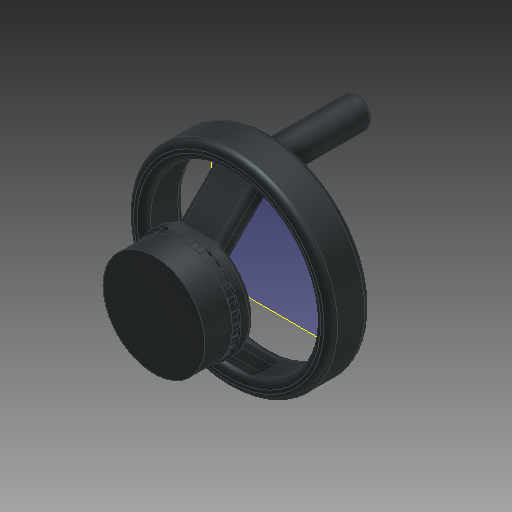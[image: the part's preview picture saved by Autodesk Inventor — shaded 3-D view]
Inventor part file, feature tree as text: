
AUTODESK INVENTOR PART (.ipt)
format: ipt  version: 2018 (Build 220112000, 112)  size: 558,080 bytes
history: native  units: mm
features: extrude x13, sketch x13, fillet x6, pattern_circular x1, chamfer x1, plane x1
ambient origin geometry x8: Origin, YZ Plane, XZ Plane, XY Plane, X Axis, Y Axis, Z Axis, Center Point
bodies: Solid1 (feature_tree)
feature tree (35):
  extrude  "Extrusion1"  Depth=20.0mm TaperAngle=0.0deg
  extrude  "Extrusion2"  Depth=5.0mm TaperAngle=0.0deg
  extrude  "Extrusion3"  Depth=5.0mm
  pattern_circular  "Circular Pattern1"  Count=30 Angle=360.0deg
  extrude  "Extrusion4"  Depth=10.0mm TaperAngle=0.0deg
  extrude  "Extrusion5"  Depth=16.0mm
  extrude  "Extrusion6"  Depth=10.0mm
  chamfer  "Chamfer1"  Distance=10.0mm
  plane  "Work Plane1"
  extrude  "Extrusion7"  Depth=2.0mm
  fillet  "Fillet1"  Radius=150.0mm
  extrude  "Extrusion8"  Depth=5.0mm TaperAngle=0.0deg
  fillet  "Fillet2"  Radius=5.0mm
  extrude  "Extrusion9"  Depth=5.0mm
  fillet  "Fillet3"  Radius=62.25mm
  extrude  "Extrusion10"  Depth=5.0mm TaperAngle=0.0deg
  fillet  "Fillet4"  Radius=4.0mm
  extrude  "Extrusion11"  Depth=4.0mm
  fillet  "Fillet5"  Radius=22.0mm
  extrude  "Extrusion12"  Depth=2.0mm TaperAngle=0.0deg
  extrude  "Extrusion13"  Depth=2.0mm
  fillet  "Fillet6"  [1 undecoded]
  sketch  "Sketch1"  dims[d0=75.0mm d1=20.0mm d2=0.0mm]
  sketch  "Sketch2"  dims[d3=76.0mm d4=5.0mm d5=0.0mm]
  sketch  "Sketch3"  dims[d7=2.5mm d8=5.0mm]
  sketch  "Sketch4"  dims[d9=5.0mm d10=0.0mm d11=300.0mm d12=360.0deg]
  sketch  "Sketch5"  dims[d14=78.0mm d15=10.0mm d16=0.0mm]
  sketch  "Sketch6"  dims[d17=16.0mm d18=16.0mm]
  sketch  "Sketch7"  dims[d19=10.0mm d20=0.0mm d21=55.0mm d22=10.0mm d23=0.0mm]
  sketch  "Sketch8"  dims[d24=10.0mm d25=2.0mm d26=45.0deg d27=50.0mm d28=150.0mm]
  sketch  "Sketch9"  dims[d29=125.0mm d30=30.0mm d31=0.0mm d32=5.0mm]
  sketch  "Sketch10"  dims[d33=61.75mm d34=0.0mm d35=5.0mm d36=62.25mm d37=0.0mm]
  sketch  "Sketch11"  dims[d38=5.0mm d39=32.0mm d40=0.0mm d41=4.0mm]
  sketch  "Sketch12"  dims[d42=32.0mm d43=0.0mm d44=4.0mm d45=22.0mm]
  sketch  "Sketch13"  dims[d46=50.0mm d47=0.0mm d48=40.0mm d49=0.0mm d50=2.0mm]
note: 1 required parameter value undecoded (feature->parameter linkage not recoverable at this tier; creation-order binding heuristic only, values carry confidence <= 0.55)
